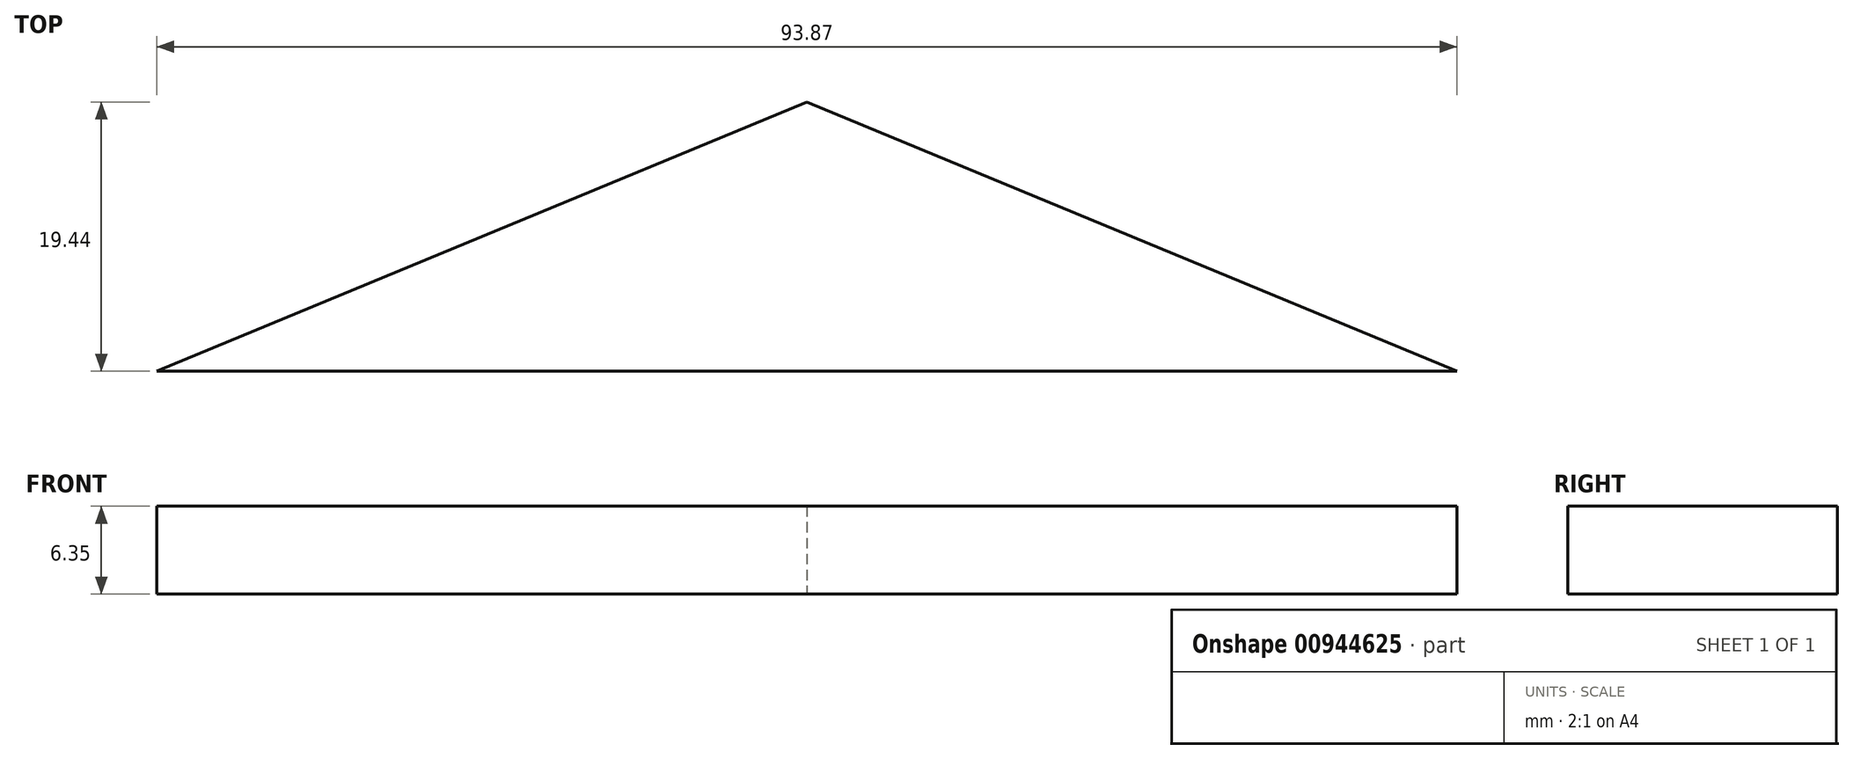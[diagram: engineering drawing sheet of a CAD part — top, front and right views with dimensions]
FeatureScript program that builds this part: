
annotation { "Feature Type Name" : "Feature", "Feature Type Description" : "" }
export const myFeature = defineFeature(function(context is Context, id is Id, definition is map)
    precondition{}
    {
        {
            var Q0;
            Q0=qCreatedBy(makeId("Top.planeOp"),FACE);
            var sketch = newSketch(context, id + "F0", { "sketchPlane" : qUnion([Q0])});
            skLineSegment(sketch, "E0", {"start": v(0, 0) * mm, "end": v(46.93, 19.44) * mm});
            skLineSegment(sketch, "E1", {"start": v(46.93, 19.44) * mm, "end": v(93.87, 0) * mm});
            skLineSegment(sketch, "E2", {"start": v(0, 0) * mm, "end": v(93.87, 0) * mm});
            skSolve(sketch);
        }
        {
            var Q0;
            Q0=makeQuery(id+"F0.imprint","IMPRINT",FACE,{"disambiguationData":[TD([[makeQuery(id+"F0.imprint","IMPRINT",EDGE,{"derivedFrom":sQuery(id+"F0.wireOp",EDGE,"E0")}),-1.0]])]});
            extrude(context, id + "F1", {"entities" : qUnion([Q0]), "depth" : 6.35 * mm, "offsetDistance" : 25.4 * mm});
        }
    });
